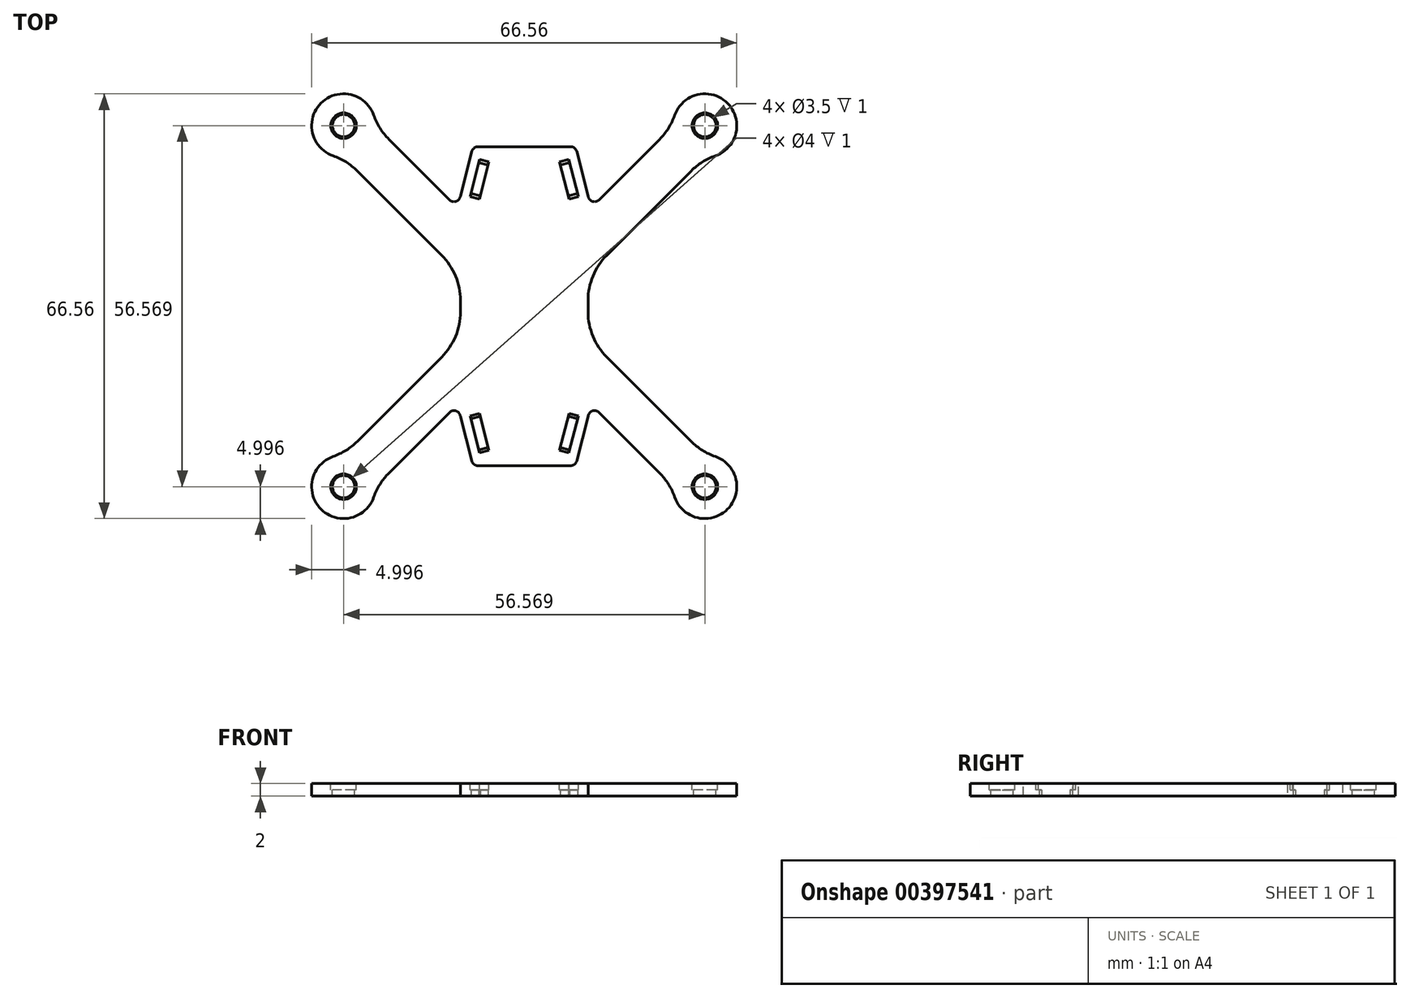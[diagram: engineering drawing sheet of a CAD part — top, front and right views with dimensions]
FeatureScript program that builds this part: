
annotation { "Feature Type Name" : "Feature", "Feature Type Description" : "" }
export const myFeature = defineFeature(function(context is Context, id is Id, definition is map)
    precondition{}
    {
        {
            var Q0;
            Q0=qCreatedBy(makeId("Top.planeOp"),FACE);
            var sketch = newSketch(context, id + "F0", { "sketchPlane" : qUnion([Q0])});
            skLineSegment(sketch, "E0.bottom", {"start": v(10, -25) * mm, "end": v(-10, -25) * mm});
            skLineSegment(sketch, "E0.top", {"start": v(10, 25) * mm, "end": v(-10, 25) * mm});
            skLineSegment(sketch, "E0.left", {"start": v(10, -25) * mm, "end": v(10, 25) * mm});
            skLineSegment(sketch, "E0.right", {"start": v(-10, -25) * mm, "end": v(-10, 25) * mm});
            skPoint(sketch, "E0.middle", {"position": v(0, 0) * mm});
            skLineSegment(sketch, "E1.bottom", {"start": v(-25.8, 30.76) * mm, "end": v(2.47, 2.47) * mm});
            skLineSegment(sketch, "E1.top", {"start": v(-30.76, 25.8) * mm, "end": v(-2.47, -2.47) * mm});
            skLineSegment(sketch, "E1.left", {"start": v(-25.8, 30.76) * mm, "end": v(-30.76, 25.8) * mm});
            skLineSegment(sketch, "E1.right", {"start": v(2.47, 2.47) * mm, "end": v(-2.47, -2.47) * mm});
            skCircle(sketch, "E2", {"center": v(-28.28, 28.28) * mm, "radius": 5 * mm});
            skCircle(sketch, "E3.1.1", {"center": v(-28.28, -28.28) * mm, "radius": 5 * mm});
            skLineSegment(sketch, "E3.1.2", {"start": v(-30.76, -25.8) * mm, "end": v(-2.47, 2.47) * mm});
            skLineSegment(sketch, "E3.1.3", {"start": v(-25.8, -30.76) * mm, "end": v(2.47, -2.47) * mm});
            skLineSegment(sketch, "E3.1.4", {"start": v(-30.76, -25.8) * mm, "end": v(-25.8, -30.76) * mm});
            skLineSegment(sketch, "E3.1.5", {"start": v(-2.47, 2.47) * mm, "end": v(2.47, -2.47) * mm});
            skCircle(sketch, "E3.2.1", {"center": v(28.28, -28.28) * mm, "radius": 5 * mm});
            skLineSegment(sketch, "E3.2.2", {"start": v(25.8, -30.76) * mm, "end": v(-2.47, -2.47) * mm});
            skLineSegment(sketch, "E3.2.3", {"start": v(30.76, -25.8) * mm, "end": v(2.47, 2.47) * mm});
            skLineSegment(sketch, "E3.2.4", {"start": v(25.8, -30.76) * mm, "end": v(30.76, -25.8) * mm});
            skLineSegment(sketch, "E3.2.5", {"start": v(-2.47, -2.47) * mm, "end": v(2.47, 2.47) * mm});
            skCircle(sketch, "E4.1.3.0", {"center": v(28.28, 28.28) * mm, "radius": 5 * mm});
            skLineSegment(sketch, "E4.3.3.0", {"start": v(30.76, 25.8) * mm, "end": v(2.47, -2.47) * mm});
            skLineSegment(sketch, "E4.6.3.0", {"start": v(25.8, 30.76) * mm, "end": v(-2.47, 2.47) * mm});
            skLineSegment(sketch, "E4.9.3.0", {"start": v(30.76, 25.8) * mm, "end": v(25.8, 30.76) * mm});
            skLineSegment(sketch, "E4.12.3.0", {"start": v(2.47, -2.47) * mm, "end": v(-2.47, 2.47) * mm});
            skSolve(sketch);
        }
        {
            var Q0;
            Q0 = qSketchRegion(id + "F0", true);
            var Q1;
            {var subQ1=sQuery(id+"F0.wireOp",EDGE,"E3.1.3");var subQ3=sQuery(id+"F0.wireOp",EDGE,"E3.2.2");var subQ4=makeQuery(id+"F0.imprint","INTERSECT",VERTEX,{"derivedFrom":[subQ1,subQ3]});Q1=makeQuery(id+"F0.imprint","IMPRINT",FACE,{"disambiguationData":[TD([[makeQuery(id+"F0.imprint","IMPRINT",EDGE,{"disambiguationData":[TD([[subQ4,-1.0]])],"derivedFrom":subQ1}),1.0]])]});}
            var Q2;
            {var subQ1=sQuery(id+"F0.wireOp",EDGE,"E1.top");var subQ3=sQuery(id+"F0.wireOp",EDGE,"E3.1.2");var subQ4=makeQuery(id+"F0.imprint","INTERSECT",VERTEX,{"derivedFrom":[subQ1,subQ3]});Q2=makeQuery(id+"F0.imprint","IMPRINT",FACE,{"disambiguationData":[TD([[makeQuery(id+"F0.imprint","IMPRINT",EDGE,{"disambiguationData":[TD([[subQ4,-1.0]])],"derivedFrom":subQ1}),1.0]])]});}
            var Q3;
            {var subQ1=sQuery(id+"F0.wireOp",EDGE,"E1.bottom");var subQ3=sQuery(id+"F0.wireOp",EDGE,"E4.6.3.0");var subQ4=makeQuery(id+"F0.imprint","INTERSECT",VERTEX,{"derivedFrom":[subQ1,subQ3]});Q3=makeQuery(id+"F0.imprint","IMPRINT",FACE,{"disambiguationData":[TD([[makeQuery(id+"F0.imprint","IMPRINT",EDGE,{"disambiguationData":[TD([[subQ4,-1.0]])],"derivedFrom":subQ1}),-1.0]])]});}
            var Q4;
            {var subQ1=sQuery(id+"F0.wireOp",EDGE,"E3.2.3");var subQ3=sQuery(id+"F0.wireOp",EDGE,"E4.3.3.0");var subQ4=makeQuery(id+"F0.imprint","INTERSECT",VERTEX,{"derivedFrom":[subQ1,subQ3]});Q4=makeQuery(id+"F0.imprint","IMPRINT",FACE,{"disambiguationData":[TD([[makeQuery(id+"F0.imprint","IMPRINT",EDGE,{"disambiguationData":[TD([[subQ4,-1.0]])],"derivedFrom":subQ1}),1.0]])]});}
            extrude(context, id + "F1", {"entities" : qUnion([Q0, Q1, Q2, Q3, Q4]), "oppositeDirection" : true, "depth" : 2 * mm});
        }
        {
            var Q0;
            Q0=makeQuery(id+"F1.opExtrude","SWEPT_EDGE",EDGE,{"disambiguationData":[OSD([sQuery(id+"F0.wireOp",EDGE,"E3.2.1"),sQuery(id+"F0.wireOp",EDGE,"E3.2.3")])]});
            var Q1;
            Q1=makeQuery(id+"F1.opExtrude","SWEPT_EDGE",EDGE,{"disambiguationData":[OSD([sQuery(id+"F0.wireOp",EDGE,"E0.left"),sQuery(id+"F0.wireOp",EDGE,"E3.2.3")])]});
            var Q2;
            Q2=makeQuery(id+"F1.opExtrude","SWEPT_EDGE",EDGE,{"disambiguationData":[OSD([sQuery(id+"F0.wireOp",EDGE,"E0.left"),sQuery(id+"F0.wireOp",EDGE,"E4.3.3.0")])]});
            var Q3;
            Q3=makeQuery(id+"F1.opExtrude","SWEPT_EDGE",EDGE,{"disambiguationData":[OSD([sQuery(id+"F0.wireOp",EDGE,"E3.2.1"),sQuery(id+"F0.wireOp",EDGE,"E3.2.2")])]});
            var Q4;
            Q4=makeQuery(id+"F1.opExtrude","SWEPT_EDGE",EDGE,{"disambiguationData":[OSD([sQuery(id+"F0.wireOp",EDGE,"E4.1.3.0"),sQuery(id+"F0.wireOp",EDGE,"E4.3.3.0")])]});
            var Q5;
            Q5=makeQuery(id+"F1.opExtrude","SWEPT_EDGE",EDGE,{"disambiguationData":[OSD([sQuery(id+"F0.wireOp",EDGE,"E3.1.1"),sQuery(id+"F0.wireOp",EDGE,"E3.1.3")])]});
            var Q6;
            Q6=makeQuery(id+"F1.opExtrude","SWEPT_EDGE",EDGE,{"disambiguationData":[OSD([sQuery(id+"F0.wireOp",EDGE,"E0.right"),sQuery(id+"F0.wireOp",EDGE,"E3.1.2")])]});
            var Q7;
            Q7=makeQuery(id+"F1.opExtrude","SWEPT_EDGE",EDGE,{"disambiguationData":[OSD([sQuery(id+"F0.wireOp",EDGE,"E0.right"),sQuery(id+"F0.wireOp",EDGE,"E1.top")])]});
            var Q8;
            Q8=makeQuery(id+"F1.opExtrude","SWEPT_EDGE",EDGE,{"disambiguationData":[OSD([sQuery(id+"F0.wireOp",EDGE,"E1.top"),sQuery(id+"F0.wireOp",EDGE,"E2")])]});
            var Q9;
            Q9=makeQuery(id+"F1.opExtrude","SWEPT_EDGE",EDGE,{"disambiguationData":[OSD([sQuery(id+"F0.wireOp",EDGE,"E3.1.1"),sQuery(id+"F0.wireOp",EDGE,"E3.1.2")])]});
            var Q10;
            Q10=makeQuery(id+"F1.opExtrude","SWEPT_EDGE",EDGE,{"disambiguationData":[OSD([sQuery(id+"F0.wireOp",EDGE,"E1.bottom"),sQuery(id+"F0.wireOp",EDGE,"E2")])]});
            var Q11;
            Q11=makeQuery(id+"F1.opExtrude","SWEPT_EDGE",EDGE,{"disambiguationData":[OSD([sQuery(id+"F0.wireOp",EDGE,"E4.1.3.0"),sQuery(id+"F0.wireOp",EDGE,"E4.6.3.0")])]});
            fillet(context, id + "F2", {"entities" : qUnion([Q0, Q1, Q2, Q3, Q4, Q5, Q6, Q7, Q8, Q9, Q10, Q11]), "radius" : 10 * mm, "tangentPropagation" : true, "allowEdgeOverflow" : false});
        }
        {
            var Q0;
            Q0=makeQuery(id+"F1.opExtrude","SWEPT_EDGE",EDGE,{"disambiguationData":[OSD([sQuery(id+"F0.wireOp",EDGE,"E0.left"),sQuery(id+"F0.wireOp",EDGE,"E3.2.2")])]});
            var Q1;
            Q1=makeQuery(id+"F1.opExtrude","SWEPT_EDGE",EDGE,{"disambiguationData":[OSD([sQuery(id+"F0.wireOp",EDGE,"E0.right"),sQuery(id+"F0.wireOp",EDGE,"E3.1.3")])]});
            var Q2;
            Q2=makeQuery(id+"F1.opExtrude","SWEPT_EDGE",EDGE,{"disambiguationData":[OSD([sQuery(id+"F0.wireOp",EDGE,"E0.left"),sQuery(id+"F0.wireOp",EDGE,"E4.6.3.0")])]});
            var Q3;
            Q3=makeQuery(id+"F1.opExtrude","SWEPT_EDGE",EDGE,{"disambiguationData":[OSD([sQuery(id+"F0.wireOp",EDGE,"E0.right"),sQuery(id+"F0.wireOp",EDGE,"E1.bottom")])]});
            fillet(context, id + "F3", {"entities" : qUnion([Q0, Q1, Q2, Q3]), "radius" : 1 * mm, "tangentPropagation" : true, "allowEdgeOverflow" : false});
        }
        {
            var Q0;
            Q0=makeQuery(id+"F1.opExtrude","SWEPT_EDGE",EDGE,{"disambiguationData":[OSD([sQuery(id+"F0.wireOp",EDGE,"E0.top"),sQuery(id+"F0.wireOp",EDGE,"E0.right")])]});
            var Q1;
            Q1=makeQuery(id+"F1.opExtrude","SWEPT_EDGE",EDGE,{"disambiguationData":[OSD([sQuery(id+"F0.wireOp",EDGE,"E0.top"),sQuery(id+"F0.wireOp",EDGE,"E0.left")])]});
            chamfer(context, id + "F4", {"entities" : qUnion([Q0, Q1]), "chamferType" : ChamferType.TWO_OFFSETS, "width1" : 8 * mm, "oppositeDirection" : true, "width2" : 2 * mm, "tangentPropagation" : true});
        }
        {
            var Q0;
            Q0=makeQuery(id+"F1.opExtrude","SWEPT_EDGE",EDGE,{"disambiguationData":[OSD([sQuery(id+"F0.wireOp",EDGE,"E0.bottom"),sQuery(id+"F0.wireOp",EDGE,"E0.right")])]});
            var Q1;
            Q1=makeQuery(id+"F1.opExtrude","SWEPT_EDGE",EDGE,{"disambiguationData":[OSD([sQuery(id+"F0.wireOp",EDGE,"E0.bottom"),sQuery(id+"F0.wireOp",EDGE,"E0.left")])]});
            chamfer(context, id + "F5", {"entities" : qUnion([Q0, Q1]), "chamferType" : ChamferType.TWO_OFFSETS, "width1" : 2 * mm, "oppositeDirection" : true, "width2" : 8 * mm, "tangentPropagation" : true});
        }
        {
            var Q0;
            {var subQ0=sQuery(id+"F0.wireOp",EDGE,"E0.bottom");Q0=makeQuery(id+"F5.opChamfer","BLEND_EDGE",EDGE,{"blendedFrom":[makeQuery(id+"F1.opExtrude","SWEPT_EDGE",EDGE,{"disambiguationData":[OSD([subQ0,sQuery(id+"F0.wireOp",EDGE,"E0.left")])]}),makeQuery(id+"F1.opExtrude","SWEPT_FACE",FACE,{"disambiguationData":[OSD([subQ0])]})],"blendedInto":[makeQuery(id+"F1.opExtrude","SWEPT_FACE",FACE,{"disambiguationData":[OSD([subQ0])]})]});}
            var Q1;
            {var subQ0=sQuery(id+"F0.wireOp",EDGE,"E0.bottom");Q1=makeQuery(id+"F5.opChamfer","BLEND_EDGE",EDGE,{"blendedFrom":[makeQuery(id+"F1.opExtrude","SWEPT_EDGE",EDGE,{"disambiguationData":[OSD([subQ0,sQuery(id+"F0.wireOp",EDGE,"E0.right")])]}),makeQuery(id+"F1.opExtrude","SWEPT_FACE",FACE,{"disambiguationData":[OSD([subQ0])]})],"blendedInto":[makeQuery(id+"F1.opExtrude","SWEPT_FACE",FACE,{"disambiguationData":[OSD([subQ0])]})]});}
            var Q2;
            {var subQ0=sQuery(id+"F0.wireOp",EDGE,"E0.top");Q2=makeQuery(id+"F4.opChamfer","BLEND_EDGE",EDGE,{"blendedFrom":[makeQuery(id+"F1.opExtrude","SWEPT_EDGE",EDGE,{"disambiguationData":[OSD([subQ0,sQuery(id+"F0.wireOp",EDGE,"E0.right")])]}),makeQuery(id+"F1.opExtrude","SWEPT_FACE",FACE,{"disambiguationData":[OSD([subQ0])]})],"blendedInto":[makeQuery(id+"F1.opExtrude","SWEPT_FACE",FACE,{"disambiguationData":[OSD([subQ0])]})]});}
            var Q3;
            {var subQ0=sQuery(id+"F0.wireOp",EDGE,"E0.top");Q3=makeQuery(id+"F4.opChamfer","BLEND_EDGE",EDGE,{"blendedFrom":[makeQuery(id+"F1.opExtrude","SWEPT_EDGE",EDGE,{"disambiguationData":[OSD([subQ0,sQuery(id+"F0.wireOp",EDGE,"E0.left")])]}),makeQuery(id+"F1.opExtrude","SWEPT_FACE",FACE,{"disambiguationData":[OSD([subQ0])]})],"blendedInto":[makeQuery(id+"F1.opExtrude","SWEPT_FACE",FACE,{"disambiguationData":[OSD([subQ0])]})]});}
            fillet(context, id + "F6", {"entities" : qUnion([Q0, Q1, Q2, Q3]), "radius" : 1 * mm, "tangentPropagation" : true, "allowEdgeOverflow" : false});
        }
        {
            var Q0;
            Q0=sQuery(id+"F0.wireOp",VERTEX,"E3.2.1.center");
            var Q1;
            Q1=sQuery(id+"F0.wireOp",VERTEX,"E2.center");
            var Q2;
            Q2=sQuery(id+"F0.wireOp",VERTEX,"E4.1.3.0.center");
            var Q3;
            Q3=sQuery(id+"F0.wireOp",VERTEX,"E3.1.1.center");
            var Q4;
            Q4=makeQuery(id+"F1.opExtrude","SWEPT_BODY",BODY,{"disambiguationData":[OSD([sQuery(id+"F0.wireOp",EDGE,"E0.bottom"),sQuery(id+"F0.wireOp",EDGE,"E0.top"),sQuery(id+"F0.wireOp",EDGE,"E0.left"),sQuery(id+"F0.wireOp",EDGE,"E0.right"),sQuery(id+"F0.wireOp",EDGE,"E1.bottom"),sQuery(id+"F0.wireOp",EDGE,"E1.top"),sQuery(id+"F0.wireOp",EDGE,"E2"),sQuery(id+"F0.wireOp",EDGE,"E3.1.1"),sQuery(id+"F0.wireOp",EDGE,"E3.1.2"),sQuery(id+"F0.wireOp",EDGE,"E3.1.3"),sQuery(id+"F0.wireOp",EDGE,"E3.2.1"),sQuery(id+"F0.wireOp",EDGE,"E3.2.2"),sQuery(id+"F0.wireOp",EDGE,"E3.2.3"),sQuery(id+"F0.wireOp",EDGE,"E4.1.3.0"),sQuery(id+"F0.wireOp",EDGE,"E4.3.3.0"),sQuery(id+"F0.wireOp",EDGE,"E4.6.3.0")])]});
            hole(context, id + "F7", {"style" : HoleStyle.C_BORE, "endStyle" : HoleEndStyle.THROUGH, "holeDiameter" : 3.5 * mm, "cBoreDiameter" : 4 * mm, "cBoreDepth" : 1 * mm, "isTappedThrough" : true, "tappedDepth" : 12 * mm, "tapClearance" : 3, "locations" : qUnion([Q0, Q1, Q2, Q3]), "scope" : qUnion([Q4])});
        }
        {
            var Q0;
            Q0=makeQuery(id+"F1.opExtrude","CAP_FACE",FACE,{"disambiguationData":[OSD([sQuery(id+"F0.wireOp",EDGE,"E0.bottom"),sQuery(id+"F0.wireOp",EDGE,"E0.top"),sQuery(id+"F0.wireOp",EDGE,"E0.left"),sQuery(id+"F0.wireOp",EDGE,"E0.right"),sQuery(id+"F0.wireOp",EDGE,"E1.bottom"),sQuery(id+"F0.wireOp",EDGE,"E1.top"),sQuery(id+"F0.wireOp",EDGE,"E2"),sQuery(id+"F0.wireOp",EDGE,"E3.1.1"),sQuery(id+"F0.wireOp",EDGE,"E3.1.2"),sQuery(id+"F0.wireOp",EDGE,"E3.1.3"),sQuery(id+"F0.wireOp",EDGE,"E3.2.1"),sQuery(id+"F0.wireOp",EDGE,"E3.2.2"),sQuery(id+"F0.wireOp",EDGE,"E3.2.3"),sQuery(id+"F0.wireOp",EDGE,"E4.1.3.0"),sQuery(id+"F0.wireOp",EDGE,"E4.3.3.0"),sQuery(id+"F0.wireOp",EDGE,"E4.6.3.0")])],"isStart":false});
            var sketch = newSketch(context, id + "F8", { "sketchPlane" : qUnion([Q0])});
            skLineSegment(sketch, "E5.bottom", {"start": v(-7.11, 22.5) * mm, "end": v(-5.66, 22.13) * mm});
            skLineSegment(sketch, "E5.top", {"start": v(-8.35, 17.66) * mm, "end": v(-6.9, 17.28) * mm});
            skLineSegment(sketch, "E5.left", {"start": v(-7.11, 22.5) * mm, "end": v(-8.35, 17.66) * mm});
            skLineSegment(sketch, "E5.right", {"start": v(-5.66, 22.13) * mm, "end": v(-6.9, 17.28) * mm});
            skLineSegment(sketch, "E6", {"start": v(0, 25) * mm, "end": v(0, -25) * mm, "construction": true});
            skLineSegment(sketch, "E7.MirrorCS", {"start": v(8.35, 17.66) * mm, "end": v(6.9, 17.28) * mm});
            skLineSegment(sketch, "E8.MirrorCS", {"start": v(7.11, 22.5) * mm, "end": v(5.66, 22.13) * mm});
            skLineSegment(sketch, "E9.MirrorCS", {"start": v(5.66, 22.13) * mm, "end": v(6.9, 17.28) * mm});
            skLineSegment(sketch, "E10.MirrorCS", {"start": v(7.11, 22.5) * mm, "end": v(8.35, 17.66) * mm});
            skLineSegment(sketch, "E11", {"start": v(-10, 0) * mm, "end": v(10, 0) * mm, "construction": true});
            skLineSegment(sketch, "E12.MirrorCS", {"start": v(-7.11, -22.5) * mm, "end": v(-8.35, -17.66) * mm});
            skLineSegment(sketch, "E13.MirrorCS", {"start": v(5.66, -22.13) * mm, "end": v(6.9, -17.28) * mm});
            skLineSegment(sketch, "E14.MirrorCS", {"start": v(-8.35, -17.66) * mm, "end": v(-6.9, -17.28) * mm});
            skLineSegment(sketch, "E15.MirrorCS", {"start": v(7.11, -22.5) * mm, "end": v(5.66, -22.13) * mm});
            skLineSegment(sketch, "E16.MirrorCS", {"start": v(7.11, -22.5) * mm, "end": v(8.35, -17.66) * mm});
            skLineSegment(sketch, "E17.MirrorCS", {"start": v(8.35, -17.66) * mm, "end": v(6.9, -17.28) * mm});
            skLineSegment(sketch, "E18.MirrorCS", {"start": v(-5.66, -22.13) * mm, "end": v(-6.9, -17.28) * mm});
            skLineSegment(sketch, "E19.MirrorCS", {"start": v(-7.11, -22.5) * mm, "end": v(-5.66, -22.13) * mm});
            skSolve(sketch);
        }
        {
            var Q0;
            Q0=makeQuery(id+"F8.imprint","IMPRINT",FACE,{"disambiguationData":[TD([[makeQuery(id+"F8.imprint","IMPRINT",EDGE,{"derivedFrom":sQuery(id+"F8.wireOp",EDGE,"E5.bottom")}),-1.0]])]});
            var Q1;
            Q1=makeQuery(id+"F8.imprint","IMPRINT",FACE,{"disambiguationData":[TD([[makeQuery(id+"F8.imprint","IMPRINT",EDGE,{"derivedFrom":sQuery(id+"F8.wireOp",EDGE,"E12.MirrorCS")}),-1.0]])]});
            var Q2;
            Q2=makeQuery(id+"F8.imprint","IMPRINT",FACE,{"disambiguationData":[TD([[makeQuery(id+"F8.imprint","IMPRINT",EDGE,{"derivedFrom":sQuery(id+"F8.wireOp",EDGE,"E13.MirrorCS")}),-1.0]])]});
            var Q3;
            Q3=makeQuery(id+"F8.imprint","IMPRINT",FACE,{"disambiguationData":[TD([[makeQuery(id+"F8.imprint","IMPRINT",EDGE,{"derivedFrom":sQuery(id+"F8.wireOp",EDGE,"E7.MirrorCS")}),-1.0]])]});
            extrude(context, id + "F9", {"entities" : qUnion([Q0, Q1, Q2, Q3]), "operationType" : NewBodyOperationType.REMOVE, "endBound" : BoundingType.THROUGH_ALL, "oppositeDirection" : true, "depth" : 25 * mm});
        }
        {
            var Q0;
            {var subQ1=sQuery(id+"F0.wireOp",EDGE,"E1.top");var subQ3=sQuery(id+"F0.wireOp",EDGE,"E3.1.2");var subQ4=makeQuery(id+"F0.imprint","INTERSECT",VERTEX,{"derivedFrom":[subQ1,subQ3]});Q0=makeQuery(id+"F0.imprint","IMPRINT",FACE,{"disambiguationData":[TD([[makeQuery(id+"F0.imprint","IMPRINT",EDGE,{"disambiguationData":[TD([[subQ4,-1.0]])],"derivedFrom":subQ1}),1.0]])]});}
            var sketch = newSketch(context, id + "F10", { "sketchPlane" : qUnion([Q0])});
            skLineSegment(sketch, "E20.0", {"start": v(-6.54, -16.68) * mm, "end": v(-5.05, -22.49) * mm});
            skLineSegment(sketch, "E20.1", {"start": v(-6.54, -16.68) * mm, "end": v(-8.96, -17.3) * mm});
            skLineSegment(sketch, "E20.2", {"start": v(-8.96, -17.3) * mm, "end": v(-7.47, -23.1) * mm});
            skLineSegment(sketch, "E20.3", {"start": v(-5.05, -22.49) * mm, "end": v(-7.47, -23.1) * mm});
            skLineSegment(sketch, "E21.0", {"start": v(6.54, -16.68) * mm, "end": v(5.05, -22.49) * mm});
            skLineSegment(sketch, "E21.1", {"start": v(6.54, -16.68) * mm, "end": v(8.96, -17.3) * mm});
            skLineSegment(sketch, "E21.2", {"start": v(8.96, -17.3) * mm, "end": v(7.47, -23.1) * mm});
            skLineSegment(sketch, "E21.3", {"start": v(5.05, -22.49) * mm, "end": v(7.47, -23.1) * mm});
            skLineSegment(sketch, "E22", {"start": v(-8.48, -17.17) * mm, "end": v(-6.99, -22.98) * mm});
            skLineSegment(sketch, "E23", {"start": v(-7.02, -16.8) * mm, "end": v(-5.54, -22.61) * mm});
            skLineSegment(sketch, "E24", {"start": v(7.02, -16.8) * mm, "end": v(5.54, -22.61) * mm});
            skLineSegment(sketch, "E25", {"start": v(8.48, -17.17) * mm, "end": v(6.99, -22.98) * mm});
            skLineSegment(sketch, "E26.MirrorCS", {"start": v(-6.54, 16.68) * mm, "end": v(-8.96, 17.3) * mm});
            skLineSegment(sketch, "E27.MirrorCS", {"start": v(5.05, 22.49) * mm, "end": v(7.47, 23.1) * mm});
            skLineSegment(sketch, "E28.MirrorCS", {"start": v(6.54, 16.68) * mm, "end": v(8.96, 17.3) * mm});
            skLineSegment(sketch, "E29.MirrorCS", {"start": v(-5.05, 22.49) * mm, "end": v(-7.47, 23.1) * mm});
            skLineSegment(sketch, "E30.MirrorCS", {"start": v(-6.54, 16.68) * mm, "end": v(-5.05, 22.49) * mm});
            skLineSegment(sketch, "E31.MirrorCS", {"start": v(-8.48, 17.17) * mm, "end": v(-6.99, 22.98) * mm});
            skLineSegment(sketch, "E32.MirrorCS", {"start": v(-8.96, 17.3) * mm, "end": v(-7.47, 23.1) * mm});
            skLineSegment(sketch, "E33.MirrorCS", {"start": v(8.48, 17.17) * mm, "end": v(6.99, 22.98) * mm});
            skLineSegment(sketch, "E34.MirrorCS", {"start": v(8.96, 17.3) * mm, "end": v(7.47, 23.1) * mm});
            skLineSegment(sketch, "E35.MirrorCS", {"start": v(6.54, 16.68) * mm, "end": v(5.05, 22.49) * mm});
            skLineSegment(sketch, "E36.MirrorCS", {"start": v(-7.02, 16.8) * mm, "end": v(-5.54, 22.61) * mm});
            skLineSegment(sketch, "E37.MirrorCS", {"start": v(7.02, 16.8) * mm, "end": v(5.54, 22.61) * mm});
            skSolve(sketch);
        }
        {
            var Q0;
            {var subQ0=sQuery(id+"F10.wireOp",EDGE,"E22");Q0=makeQuery(id+"F10.imprint","IMPRINT",FACE,{"disambiguationData":[TD([[makeQuery(id+"F10.imprint","IMPRINT",EDGE,{"derivedFrom":subQ0}),1.0]])]});}
            var Q1;
            {var subQ0=sQuery(id+"F10.wireOp",EDGE,"E24");Q1=makeQuery(id+"F10.imprint","IMPRINT",FACE,{"disambiguationData":[TD([[makeQuery(id+"F10.imprint","IMPRINT",EDGE,{"derivedFrom":subQ0}),1.0]])]});}
            var Q2;
            {var subQ0=sQuery(id+"F10.wireOp",EDGE,"E31.MirrorCS");Q2=makeQuery(id+"F10.imprint","IMPRINT",FACE,{"disambiguationData":[TD([[makeQuery(id+"F10.imprint","IMPRINT",EDGE,{"derivedFrom":subQ0}),-1.0]])]});}
            var Q3;
            {var subQ0=sQuery(id+"F10.wireOp",EDGE,"E33.MirrorCS");Q3=makeQuery(id+"F10.imprint","IMPRINT",FACE,{"disambiguationData":[TD([[makeQuery(id+"F10.imprint","IMPRINT",EDGE,{"derivedFrom":subQ0}),1.0]])]});}
            extrude(context, id + "F11", {"entities" : qUnion([Q0, Q1, Q2, Q3]), "operationType" : NewBodyOperationType.REMOVE, "oppositeDirection" : true, "depth" : 1 * mm});
        }
    });
